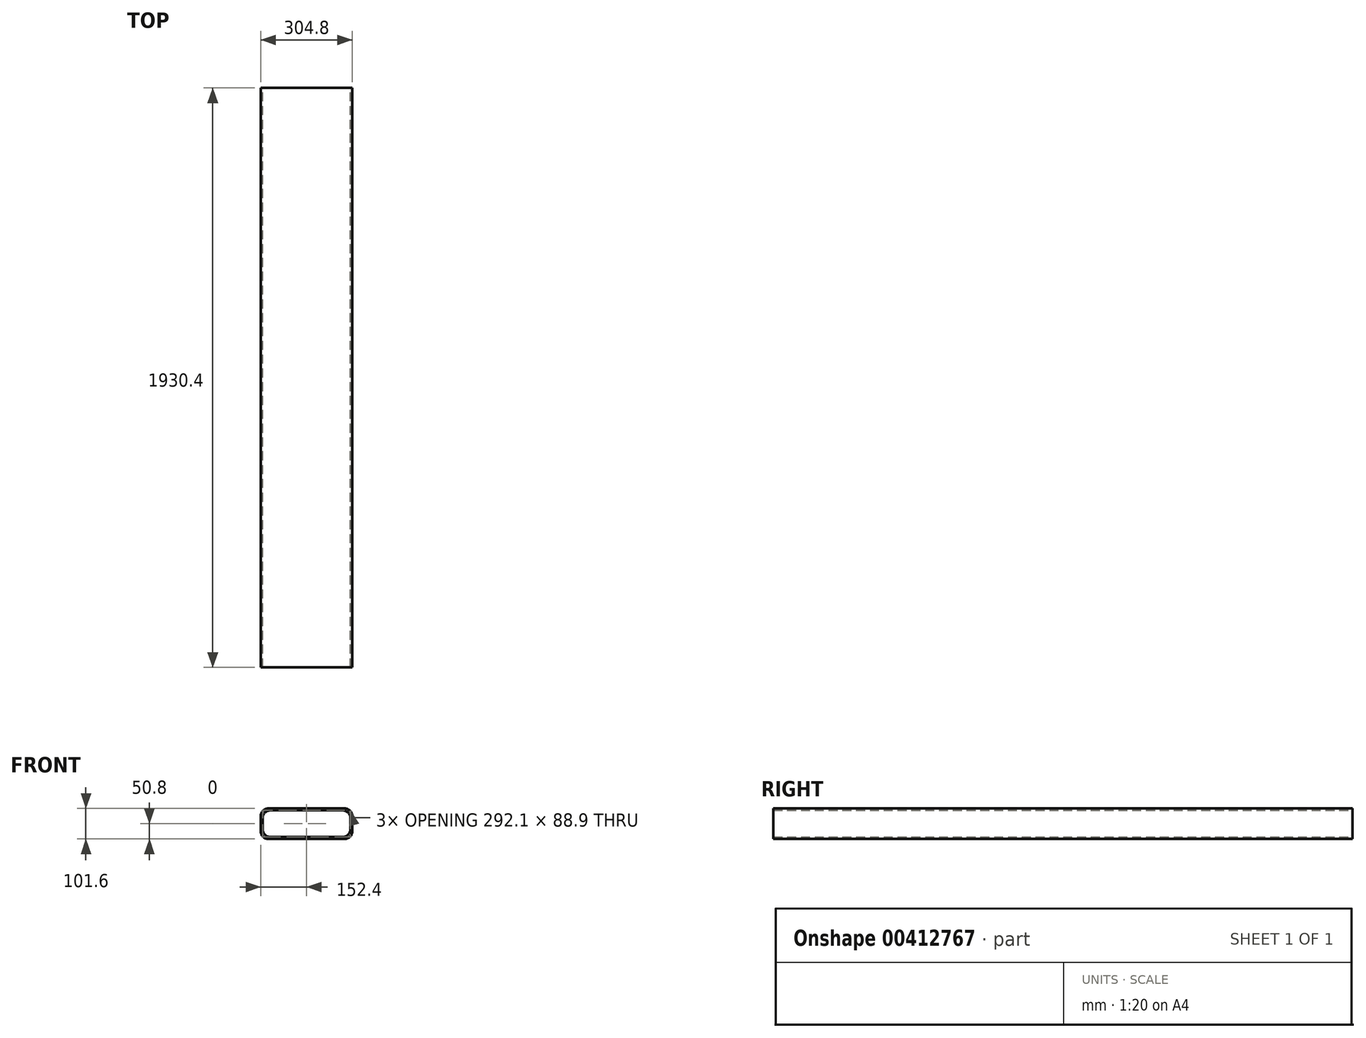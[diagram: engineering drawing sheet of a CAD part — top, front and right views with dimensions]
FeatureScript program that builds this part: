
annotation { "Feature Type Name" : "Feature", "Feature Type Description" : "" }
export const myFeature = defineFeature(function(context is Context, id is Id, definition is map)
    precondition{}
    {
        {
            var Q0;
            Q0=qCreatedBy(makeId("Front.planeOp"),FACE);
            var sketch = newSketch(context, id + "F0", { "sketchPlane" : qUnion([Q0])});
            skLineSegment(sketch, "E0.bottom", {"start": v(25.4, 0) * mm, "end": v(279.4, 0) * mm});
            skLineSegment(sketch, "E0.top", {"start": v(25.4, 101.6) * mm, "end": v(279.4, 101.6) * mm});
            skLineSegment(sketch, "E0.left", {"start": v(0, 25.4) * mm, "end": v(0, 76.2) * mm});
            skLineSegment(sketch, "E0.right", {"start": v(304.8, 25.4) * mm, "end": v(304.8, 76.2) * mm});
            skLineSegment(sketch, "E1.bottom", {"start": v(31.75, 6.35) * mm, "end": v(273.05, 6.35) * mm});
            skLineSegment(sketch, "E1.top", {"start": v(31.75, 95.25) * mm, "end": v(273.05, 95.25) * mm});
            skLineSegment(sketch, "E1.left", {"start": v(6.35, 31.75) * mm, "end": v(6.35, 69.85) * mm});
            skLineSegment(sketch, "E1.right", {"start": v(298.45, 31.75) * mm, "end": v(298.45, 69.85) * mm});
            skPoint(sketch, "E2.visualSharp", {"position": v(0, 101.6) * mm});
            skArc(sketch, "E2.filletArc", {"start": v(25.4, 101.6) * mm, "mid": v(7.44, 94.16) * mm, "end": v(0, 76.2) * mm});
            skPoint(sketch, "E3.visualSharp", {"position": v(6.35, 95.25) * mm});
            skArc(sketch, "E3.filletArc", {"start": v(31.75, 95.25) * mm, "mid": v(13.79, 87.81) * mm, "end": v(6.35, 69.85) * mm});
            skPoint(sketch, "E4.visualSharp", {"position": v(304.8, 101.6) * mm});
            skArc(sketch, "E4.filletArc", {"start": v(304.8, 76.2) * mm, "mid": v(297.36, 94.16) * mm, "end": v(279.4, 101.6) * mm});
            skPoint(sketch, "E5.visualSharp", {"position": v(298.45, 95.25) * mm});
            skArc(sketch, "E5.filletArc", {"start": v(298.45, 69.85) * mm, "mid": v(291.01, 87.81) * mm, "end": v(273.05, 95.25) * mm});
            skPoint(sketch, "E6.visualSharp", {"position": v(304.8, 0) * mm});
            skArc(sketch, "E6.filletArc", {"start": v(279.4, 0) * mm, "mid": v(297.36, 7.44) * mm, "end": v(304.8, 25.4) * mm});
            skPoint(sketch, "E7.visualSharp", {"position": v(298.45, 6.35) * mm});
            skArc(sketch, "E7.filletArc", {"start": v(273.05, 6.35) * mm, "mid": v(291.01, 13.79) * mm, "end": v(298.45, 31.75) * mm});
            skPoint(sketch, "E8.visualSharp", {"position": v(6.35, 6.35) * mm});
            skArc(sketch, "E8.filletArc", {"start": v(6.35, 31.75) * mm, "mid": v(13.79, 13.79) * mm, "end": v(31.75, 6.35) * mm});
            skPoint(sketch, "E9.visualSharp", {"position": v(0, 0) * mm});
            skArc(sketch, "E9.filletArc", {"start": v(0, 25.4) * mm, "mid": v(7.44, 7.44) * mm, "end": v(25.4, 0) * mm});
            skSolve(sketch);
        }
        {
            var Q0;
            Q0 = qSketchRegion(id + "F0", true);
            extrude(context, id + "F1", {"entities" : qUnion([Q0]), "depth" : 1930.4 * mm, "offsetDistance" : 25.4 * mm});
        }
    });
